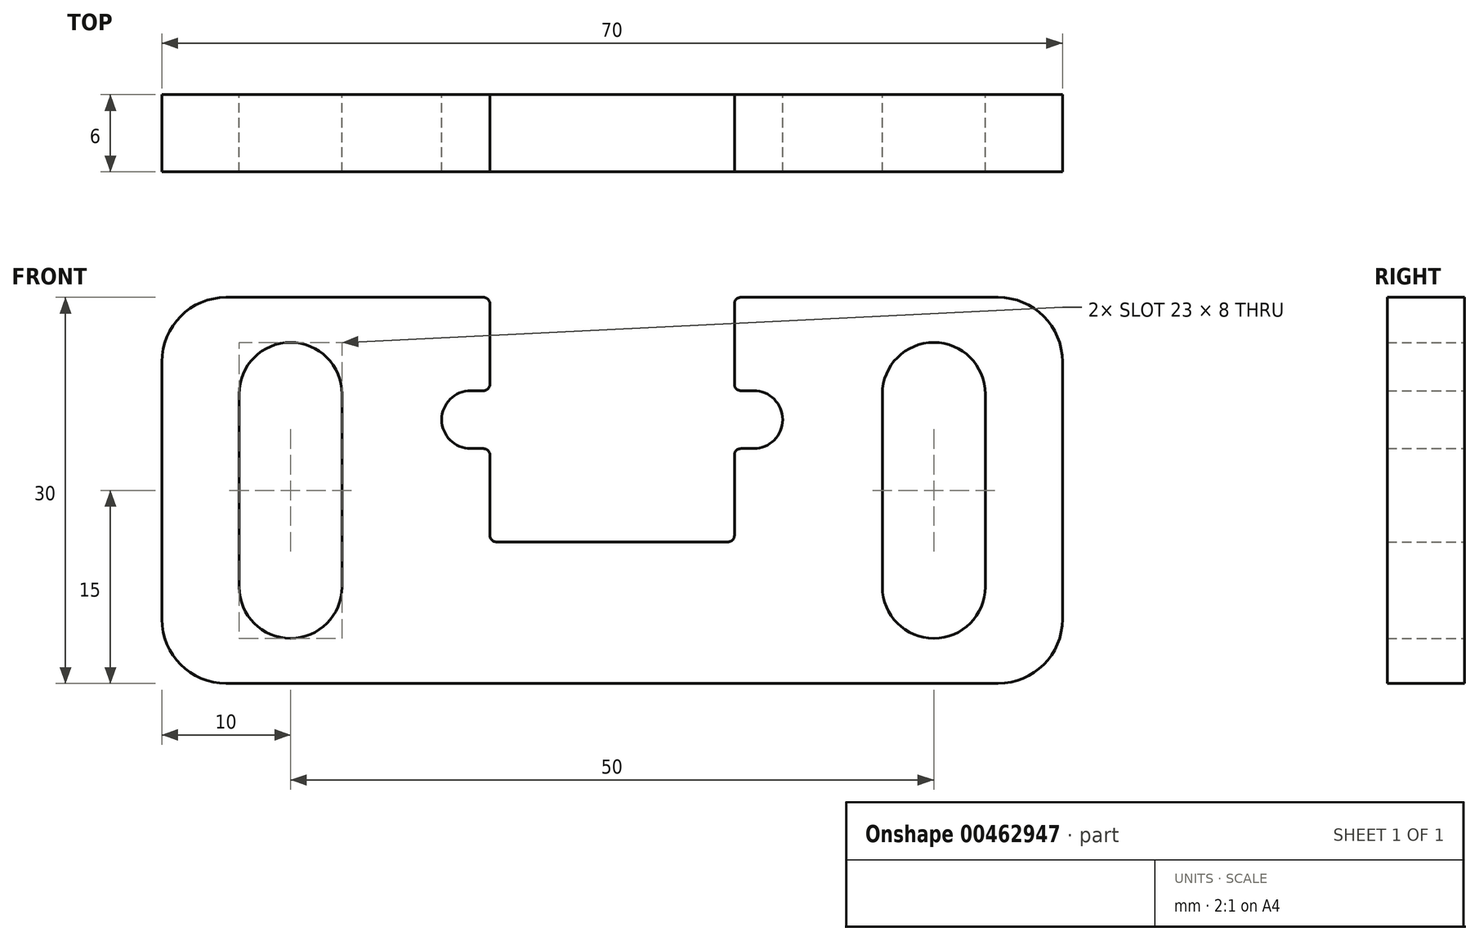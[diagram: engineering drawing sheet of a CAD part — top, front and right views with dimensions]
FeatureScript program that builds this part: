
annotation { "Feature Type Name" : "Feature", "Feature Type Description" : "" }
export const myFeature = defineFeature(function(context is Context, id is Id, definition is map)
    precondition{}
    {
        {
            var Q0;
            Q0=qCreatedBy(makeId("Front.planeOp"),FACE);
            var sketch = newSketch(context, id + "F0", { "sketchPlane" : qUnion([Q0])});
            skLineSegment(sketch, "E0.bottom", {"start": v(-17, 9.5) * mm, "end": v(-10, 9.5) * mm, "construction": true});
            skLineSegment(sketch, "E0.top", {"start": v(-9, -9.5) * mm, "end": v(9, -9.5) * mm, "construction": true});
            skLineSegment(sketch, "E0.left", {"start": v(-17, 9.5) * mm, "end": v(-17, -9.5) * mm, "construction": true});
            skLineSegment(sketch, "E0.right", {"start": v(17, 9.5) * mm, "end": v(17, -9.5) * mm, "construction": true});
            skLineSegment(sketch, "E1", {"start": v(-9.5, -9.5) * mm, "end": v(0, -9.5) * mm});
            skLineSegment(sketch, "E2", {"start": v(-17, 0) * mm, "end": v(-11, 0) * mm, "construction": true});
            skCircle(sketch, "E3", {"center": v(-11, 0) * mm, "radius": 2.25 * mm, "construction": true});
            skLineSegment(sketch, "E4", {"start": v(-11, 2.25) * mm, "end": v(-10, 2.25) * mm});
            skLineSegment(sketch, "E5", {"start": v(-11, -2.25) * mm, "end": v(-10, -2.25) * mm});
            skArc(sketch, "E6", {"start": v(-11, 2.25) * mm, "mid": v(-13.25, 0) * mm, "end": v(-11, -2.25) * mm});
            skLineSegment(sketch, "E7", {"start": v(-9.5, 9) * mm, "end": v(-9.5, 2.75) * mm});
            skLineSegment(sketch, "E8", {"start": v(-9.5, -2.75) * mm, "end": v(-9.5, -9) * mm});
            skLineSegment(sketch, "E9.MirrorCS", {"start": v(9.5, 9) * mm, "end": v(9.5, 2.75) * mm});
            skArc(sketch, "E10.MirrorCS", {"start": v(11, 2.25) * mm, "mid": v(13.25, 0) * mm, "end": v(11, -2.25) * mm});
            skLineSegment(sketch, "E11.MirrorCS", {"start": v(11, 2.25) * mm, "end": v(10, 2.25) * mm});
            skLineSegment(sketch, "E12.MirrorCS", {"start": v(9.5, -2.75) * mm, "end": v(9.5, -9) * mm});
            skLineSegment(sketch, "E13.MirrorCS", {"start": v(11, -2.25) * mm, "end": v(10, -2.25) * mm});
            skLineSegment(sketch, "E14.MirrorCS", {"start": v(9.5, -9.5) * mm, "end": v(0, -9.5) * mm});
            skLineSegment(sketch, "E15", {"start": v(-25, 2) * mm, "end": v(-25, -13) * mm, "construction": true});
            skCircle(sketch, "E16", {"center": v(-25, 2) * mm, "radius": 4 * mm, "construction": true});
            skCircle(sketch, "E17", {"center": v(-25, -13) * mm, "radius": 4 * mm, "construction": true});
            skLineSegment(sketch, "E18", {"start": v(-29, 2) * mm, "end": v(-29, -13) * mm});
            skLineSegment(sketch, "E19", {"start": v(-21, 2) * mm, "end": v(-21, -13) * mm});
            skArc(sketch, "E20", {"start": v(-29, 2) * mm, "mid": v(-25, 6) * mm, "end": v(-21, 2) * mm});
            skArc(sketch, "E21", {"start": v(-29, -13) * mm, "mid": v(-25, -17) * mm, "end": v(-21, -13) * mm});
            skLineSegment(sketch, "E22.MirrorCS", {"start": v(29, 2) * mm, "end": v(29, -13) * mm});
            skLineSegment(sketch, "E23.MirrorCS", {"start": v(21, 2) * mm, "end": v(21, -13) * mm});
            skArc(sketch, "E24.MirrorCS", {"start": v(29, -13) * mm, "mid": v(25, -17) * mm, "end": v(21, -13) * mm});
            skArc(sketch, "E25.MirrorCS", {"start": v(29, 2) * mm, "mid": v(25, 6) * mm, "end": v(21, 2) * mm});
            skLineSegment(sketch, "E26", {"start": v(0, -20.5) * mm, "end": v(-30, -20.5) * mm});
            skLineSegment(sketch, "E27", {"start": v(-35, -15.5) * mm, "end": v(-35, 4.5) * mm});
            skLineSegment(sketch, "E28", {"start": v(-30, 9.5) * mm, "end": v(-9.5, 9.5) * mm});
            skLineSegment(sketch, "E29.MirrorCS", {"start": v(0, -20.5) * mm, "end": v(30, -20.5) * mm});
            skLineSegment(sketch, "E30.MirrorCS", {"start": v(35, -15.5) * mm, "end": v(35, 4.5) * mm});
            skLineSegment(sketch, "E31.MirrorCS", {"start": v(30, 9.5) * mm, "end": v(10, 9.5) * mm});
            skPoint(sketch, "E32.visualSharp", {"position": v(-35, 9.5) * mm});
            skArc(sketch, "E32.filletArc", {"start": v(-30, 9.5) * mm, "mid": v(-33.54, 8.04) * mm, "end": v(-35, 4.5) * mm});
            skPoint(sketch, "E33.visualSharp", {"position": v(-35, -20.5) * mm});
            skArc(sketch, "E33.filletArc", {"start": v(-35, -15.5) * mm, "mid": v(-33.54, -19.04) * mm, "end": v(-30, -20.5) * mm});
            skPoint(sketch, "E34.visualSharp", {"position": v(35, -20.5) * mm});
            skArc(sketch, "E34.filletArc", {"start": v(30, -20.5) * mm, "mid": v(33.54, -19.04) * mm, "end": v(35, -15.5) * mm});
            skPoint(sketch, "E35.visualSharp", {"position": v(35, 9.5) * mm});
            skArc(sketch, "E35.filletArc", {"start": v(35, 4.5) * mm, "mid": v(33.54, 8.04) * mm, "end": v(30, 9.5) * mm});
            skPoint(sketch, "E36.visualSharp", {"position": v(-9.5, 2.25) * mm});
            skArc(sketch, "E36.filletArc", {"start": v(-10, 2.25) * mm, "mid": v(-9.65, 2.4) * mm, "end": v(-9.5, 2.75) * mm});
            skPoint(sketch, "E37.visualSharp", {"position": v(-9.5, -2.25) * mm});
            skArc(sketch, "E37.filletArc", {"start": v(-9.5, -2.75) * mm, "mid": v(-9.65, -2.4) * mm, "end": v(-10, -2.25) * mm});
            skPoint(sketch, "E38.visualSharp", {"position": v(9.5, -2.25) * mm});
            skArc(sketch, "E38.filletArc", {"start": v(10, -2.25) * mm, "mid": v(9.65, -2.4) * mm, "end": v(9.5, -2.75) * mm});
            skPoint(sketch, "E39.visualSharp", {"position": v(9.5, 2.25) * mm});
            skArc(sketch, "E39.filletArc", {"start": v(9.5, 2.75) * mm, "mid": v(9.65, 2.4) * mm, "end": v(10, 2.25) * mm});
            skPoint(sketch, "E40.newPointA", {"position": v(-9.5, -9.5) * mm});
            skPoint(sketch, "E40.newPointB", {"position": v(-17, -9.5) * mm});
            skArc(sketch, "E40.filletArc", {"start": v(-9.5, -9) * mm, "mid": v(-9.35, -9.35) * mm, "end": v(-9, -9.5) * mm});
            skPoint(sketch, "E41.newPointA", {"position": v(9.5, -9.5) * mm});
            skPoint(sketch, "E41.newPointB", {"position": v(17, -9.5) * mm});
            skArc(sketch, "E41.filletArc", {"start": v(9, -9.5) * mm, "mid": v(9.35, -9.35) * mm, "end": v(9.5, -9) * mm});
            skPoint(sketch, "E42.newPointA", {"position": v(17, 9.5) * mm});
            skPoint(sketch, "E42.newPointB", {"position": v(-9.5, 9.5) * mm});
            skArc(sketch, "E42.filletArc", {"start": v(-9.5, 9) * mm, "mid": v(-9.65, 9.35) * mm, "end": v(-10, 9.5) * mm});
            skPoint(sketch, "E43.visualSharp", {"position": v(9.5, 9.5) * mm});
            skArc(sketch, "E43.filletArc", {"start": v(10, 9.5) * mm, "mid": v(9.65, 9.35) * mm, "end": v(9.5, 9) * mm});
            skSolve(sketch);
        }
        {
            var Q0;
            Q0=makeQuery(id+"F0.imprint","IMPRINT",FACE,{"disambiguationData":[TD([[makeQuery(id+"F0.imprint","IMPRINT",EDGE,{"derivedFrom":sQuery(id+"F0.wireOp",EDGE,"E1")}),-1.0]])]});
            extrude(context, id + "F1", {"entities" : qUnion([Q0]), "depth" : 6 * mm});
        }
    });
